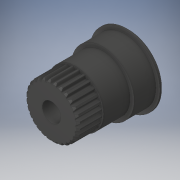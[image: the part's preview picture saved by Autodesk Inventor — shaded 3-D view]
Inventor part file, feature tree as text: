
AUTODESK INVENTOR PART (.ipt)
format: ipt  version: 2019 (Build 230136000, 136)  size: 558,080 bytes
history: native  units: in
note: dims shown in document units (in); Inventor stores cm internally (conversion verified against a paired STEP export)
features: chamfer x1
ambient origin geometry x8: Origin, YZ Plane, XZ Plane, XY Plane, X Axis, Y Axis, Z Axis, Center Point
bodies: Solid1 (feature_tree)
feature tree (1):
  chamfer  "Chamfer1"  [1 undecoded]
note: 1 required parameter value undecoded (feature->parameter linkage not recoverable at this tier; creation-order binding heuristic only, values carry confidence <= 0.55)
